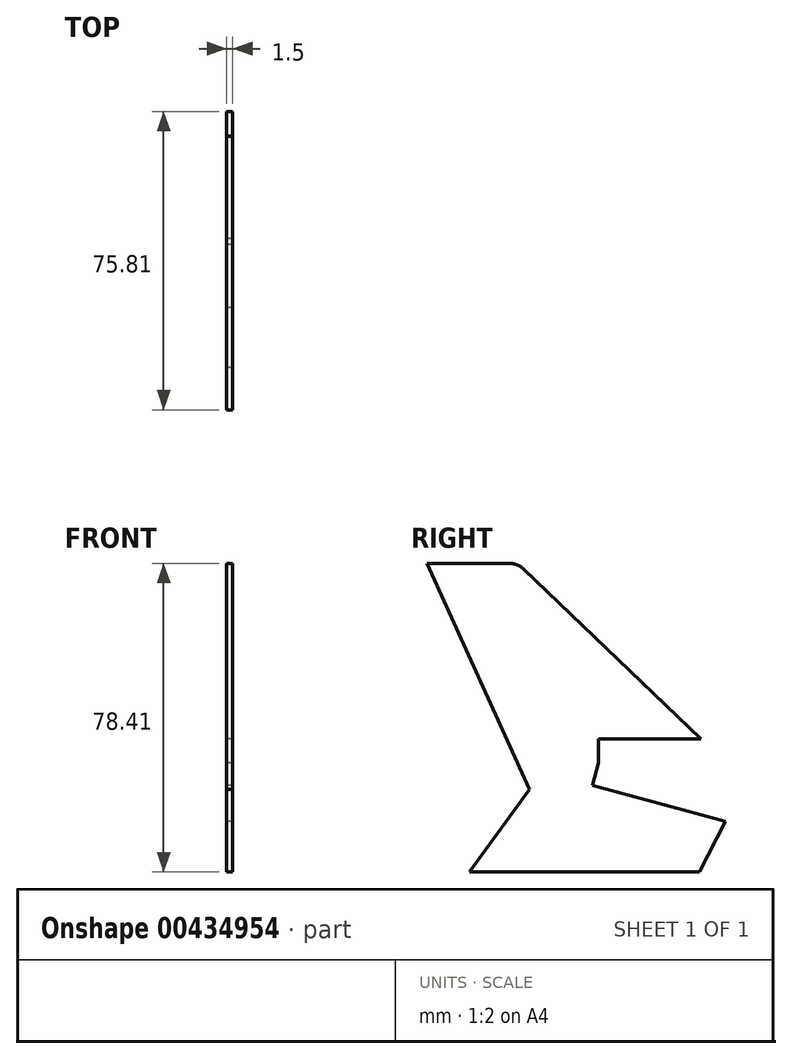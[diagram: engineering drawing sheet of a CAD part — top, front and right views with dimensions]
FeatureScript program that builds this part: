
annotation { "Feature Type Name" : "Feature", "Feature Type Description" : "" }
export const myFeature = defineFeature(function(context is Context, id is Id, definition is map)
    precondition{}
    {
        {
            var Q0;
            Q0=qCreatedBy(makeId("Right.planeOp"),FACE);
            var sketch = newSketch(context, id + "F0", { "sketchPlane" : qUnion([Q0])});
            skLineSegment(sketch, "E0", {"start": v(0, 0) * mm, "end": v(-15.28, -21.03) * mm});
            skLineSegment(sketch, "E1", {"start": v(-15.28, -21.03) * mm, "end": v(43.22, -21.03) * mm});
            skLineSegment(sketch, "E2", {"start": v(43.22, -21.03) * mm, "end": v(49.8, -8.11) * mm});
            skLineSegment(sketch, "E3", {"start": v(49.8, -8.11) * mm, "end": v(16, 0.94) * mm});
            skLineSegment(sketch, "E4", {"start": v(16, 0.94) * mm, "end": v(17.55, 6.74) * mm});
            skLineSegment(sketch, "E5", {"start": v(17.55, 6.74) * mm, "end": v(17.55, 12.74) * mm});
            skLineSegment(sketch, "E6", {"start": v(17.55, 12.74) * mm, "end": v(43.55, 12.74) * mm});
            skLineSegment(sketch, "E7", {"start": v(43.55, 12.74) * mm, "end": v(-1.56, 55.99) * mm});
            skLineSegment(sketch, "E8", {"start": v(-5.02, 57.38) * mm, "end": v(-26, 57.38) * mm});
            skLineSegment(sketch, "E9", {"start": v(-26, 57.38) * mm, "end": v(0, 0) * mm});
            skPoint(sketch, "E10.visualSharp", {"position": v(-3, 57.38) * mm});
            skArc(sketch, "E10.filletArc", {"start": v(-1.56, 55.99) * mm, "mid": v(-3.15, 57.02) * mm, "end": v(-5.02, 57.38) * mm});
            skSolve(sketch);
        }
        {
            var Q0;
            Q0 = qSketchRegion(id + "F0", true);
            extrude(context, id + "F1", {"entities" : qUnion([Q0]), "depth" : 1.5 * mm});
        }
    });
